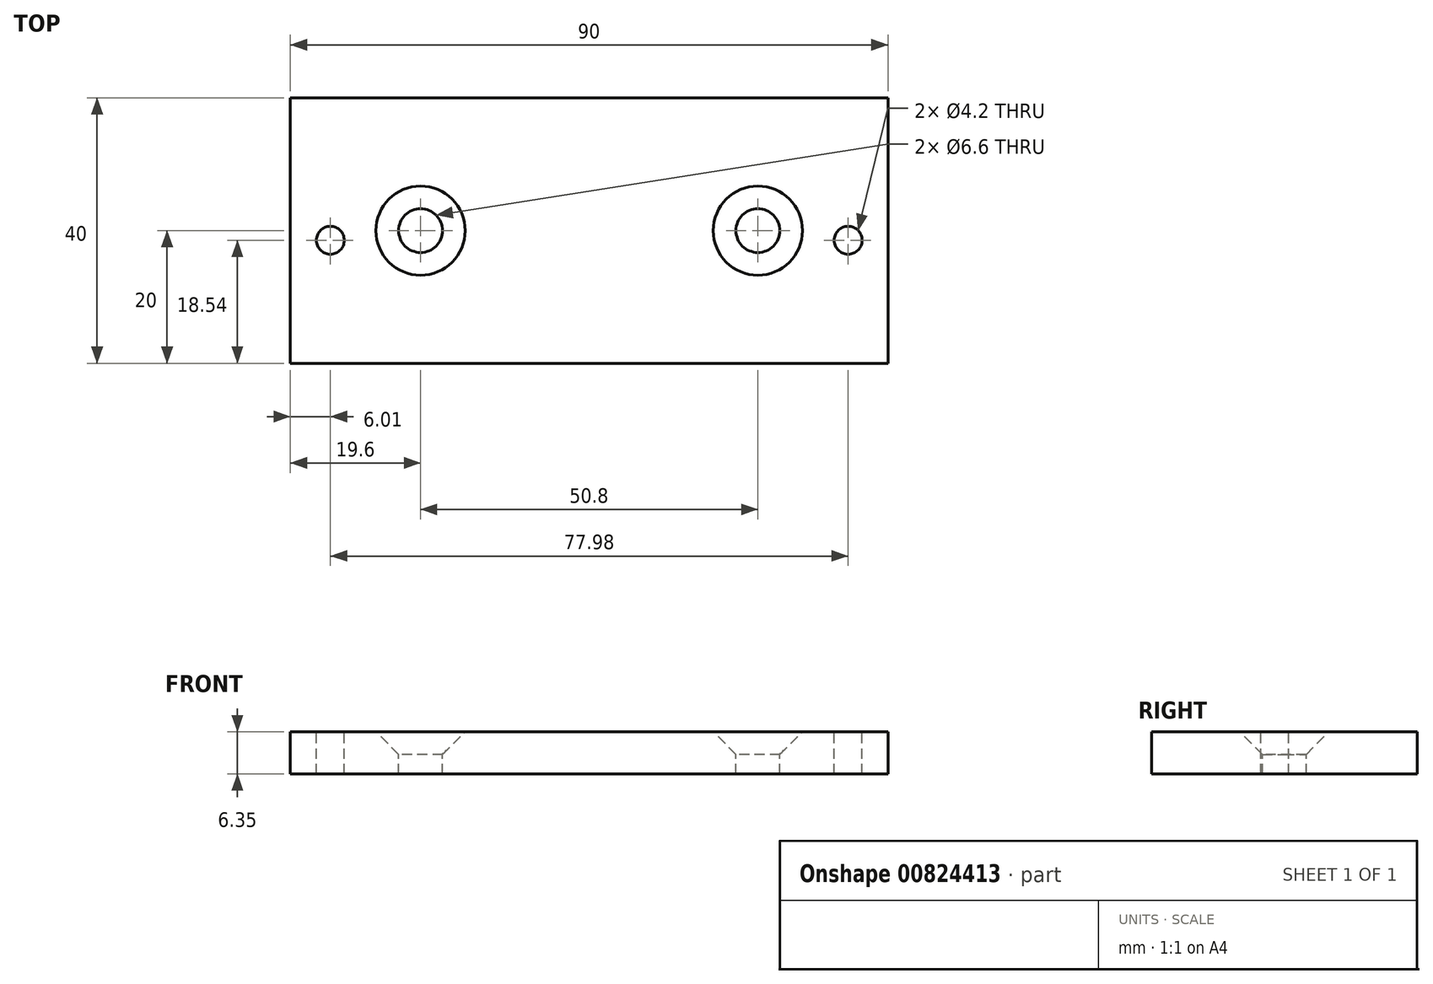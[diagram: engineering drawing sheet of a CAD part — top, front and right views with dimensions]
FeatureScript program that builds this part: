
annotation { "Feature Type Name" : "Feature", "Feature Type Description" : "" }
export const myFeature = defineFeature(function(context is Context, id is Id, definition is map)
    precondition{}
    {
        {
            var Q0;
            Q0=qCreatedBy(makeId("Top.planeOp"),FACE);
            var sketch = newSketch(context, id + "F0", { "sketchPlane" : qUnion([Q0])});
            skLineSegment(sketch, "E0.bottom", {"start": v(45, -20) * mm, "end": v(-45, -20) * mm});
            skLineSegment(sketch, "E0.top", {"start": v(45, 20) * mm, "end": v(-45, 20) * mm});
            skLineSegment(sketch, "E0.left", {"start": v(45, -20) * mm, "end": v(45, 20) * mm});
            skLineSegment(sketch, "E0.right", {"start": v(-45, -20) * mm, "end": v(-45, 20) * mm});
            skPoint(sketch, "E0.middle", {"position": v(0, 0) * mm});
            skSolve(sketch);
        }
        {
            var Q0;
            Q0=makeQuery(id+"F0.imprint","IMPRINT",FACE,{"disambiguationData":[TD([[makeQuery(id+"F0.imprint","IMPRINT",EDGE,{"derivedFrom":sQuery(id+"F0.wireOp",EDGE,"E0.bottom")}),-1.0]])]});
            extrude(context, id + "F1", {"entities" : qUnion([Q0]), "depth" : 6.35 * mm, "offsetDistance" : 25 * mm});
        }
        {
            var Q0;
            Q0=makeQuery(id+"F1.opExtrude","CAP_FACE",FACE,{"disambiguationData":[OSD([sQuery(id+"F0.wireOp",EDGE,"E0.bottom"),sQuery(id+"F0.wireOp",EDGE,"E0.top"),sQuery(id+"F0.wireOp",EDGE,"E0.left"),sQuery(id+"F0.wireOp",EDGE,"E0.right")])],"isStart":false});
            var sketch = newSketch(context, id + "F2", { "sketchPlane" : qUnion([Q0])});
            skPoint(sketch, "E1", {"position": v(-39, -1.46) * mm});
            skPoint(sketch, "E2", {"position": v(39, -1.46) * mm});
            skPoint(sketch, "E3", {"position": v(-25.4, 0) * mm});
            skPoint(sketch, "E4", {"position": v(25.4, 0) * mm});
            skLineSegment(sketch, "E5", {"start": v(-39, -1.46) * mm, "end": v(39, -1.46) * mm, "construction": true});
            skPoint(sketch, "E6", {"position": v(0, -1.46) * mm});
            skLineSegment(sketch, "E7", {"start": v(-25.4, 0) * mm, "end": v(25.4, 0) * mm});
            skSolve(sketch);
        }
        {
            var Q0;
            Q0=sQuery(id+"F2.wireOp",VERTEX,"E1");
            var Q1;
            Q1=sQuery(id+"F2.wireOp",VERTEX,"E2");
            var Q2;
            Q2=makeQuery(id+"F1.opExtrude","SWEPT_BODY",BODY,{"disambiguationData":[OSD([sQuery(id+"F0.wireOp",EDGE,"E0.bottom"),sQuery(id+"F0.wireOp",EDGE,"E0.top"),sQuery(id+"F0.wireOp",EDGE,"E0.left"),sQuery(id+"F0.wireOp",EDGE,"E0.right")])]});
            hole(context, id + "F3", {"style" : HoleStyle.SIMPLE, "endStyle" : HoleEndStyle.THROUGH, "standardTappedOrClearance" : lookupTablePath({ "standard" : "ISO", "engagement" : "75%", "pitch" : "0.8 mm", "size" : "M5", "type" : "Tapped" }), "standardBlindInLast" : lookupTablePath({ "standard" : "ISO", "engagement" : "75%", "pitch" : "0.8 mm", "size" : "M5", "type" : "Tapped" }), "holeDiameter" : 4.2 * mm, "majorDiameter" : 5 * mm, "showTappedDepth" : true, "isTappedThrough" : true, "tappedDepth" : 12 * mm, "tapClearance" : 3, "locations" : qUnion([Q0, Q1]), "scope" : qUnion([Q2])});
        }
        {
            var Q0;
            Q0=sQuery(id+"F2.wireOp",VERTEX,"E3");
            var Q1;
            Q1=sQuery(id+"F2.wireOp",VERTEX,"E4");
            var Q2;
            Q2=makeQuery(id+"F1.opExtrude","SWEPT_BODY",BODY,{"disambiguationData":[OSD([sQuery(id+"F0.wireOp",EDGE,"E0.bottom"),sQuery(id+"F0.wireOp",EDGE,"E0.top"),sQuery(id+"F0.wireOp",EDGE,"E0.left"),sQuery(id+"F0.wireOp",EDGE,"E0.right")])]});
            hole(context, id + "F4", {"style" : HoleStyle.C_SINK, "endStyle" : HoleEndStyle.THROUGH, "standardTappedOrClearance" : lookupTablePath({ "standard" : "ISO", "fit" : "Normal", "size" : "M6", "type" : "Clearance" }), "standardBlindInLast" : lookupTablePath({ "fit" : "Standard", "standard" : "ISO", "size" : "M6", "type" : "Clearance" }), "holeDiameter" : 6.6 * mm, "cSinkDiameter" : 13.44 * mm, "cSinkAngle" : 90 * degree, "majorDiameter" : 5 * mm, "isTappedThrough" : true, "tappedDepth" : 12 * mm, "tapClearance" : 3, "locations" : qUnion([Q0, Q1]), "scope" : qUnion([Q2])});
        }
    });
